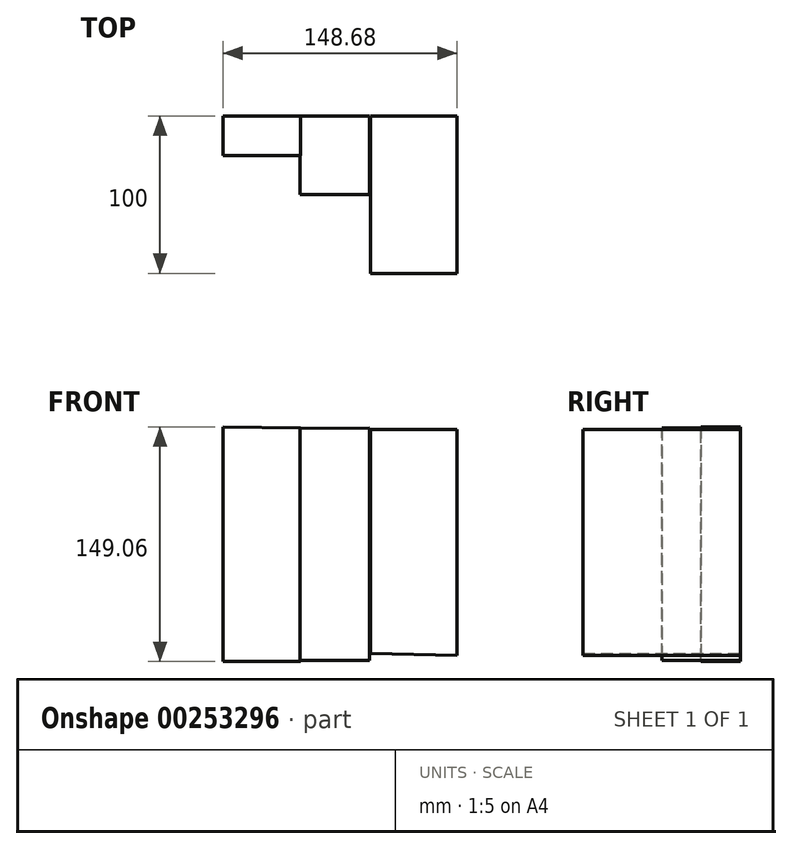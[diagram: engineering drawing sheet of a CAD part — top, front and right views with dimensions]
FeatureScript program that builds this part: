
annotation { "Feature Type Name" : "Feature", "Feature Type Description" : "" }
export const myFeature = defineFeature(function(context is Context, id is Id, definition is map)
    precondition{}
    {
        {
            var Q0;
            Q0=qCreatedBy(makeId("Front.planeOp"),FACE);
            var sketch = newSketch(context, id + "F0", { "sketchPlane" : qUnion([Q0])});
            skLineSegment(sketch, "E0", {"start": v(-74.94, 75.14) * mm, "end": v(-74.94, -73.92) * mm});
            skLineSegment(sketch, "E1", {"start": v(-74.94, -73.92) * mm, "end": v(-25.73, -73.92) * mm});
            skLineSegment(sketch, "E2", {"start": v(-25.73, -73.92) * mm, "end": v(-25.73, 74.53) * mm});
            skLineSegment(sketch, "E3", {"start": v(-25.73, 74.53) * mm, "end": v(-74.94, 75.14) * mm});
            skSolve(sketch);
        }
        {
            var Q0;
            Q0=qCreatedBy(makeId("Front.planeOp"),FACE);
            var sketch = newSketch(context, id + "F1", { "sketchPlane" : qUnion([Q0])});
            skLineSegment(sketch, "E4", {"start": v(-25.93, 74.12) * mm, "end": v(-25.93, -73.1) * mm});
            skLineSegment(sketch, "E5", {"start": v(-25.93, -73.1) * mm, "end": v(17.97, -73.1) * mm});
            skLineSegment(sketch, "E6", {"start": v(17.97, -73.1) * mm, "end": v(17.97, 74.33) * mm});
            skLineSegment(sketch, "E7", {"start": v(17.97, 74.33) * mm, "end": v(-25.93, 74.12) * mm});
            skSolve(sketch);
        }
        {
            var Q0;
            Q0=qCreatedBy(makeId("Front.planeOp"),FACE);
            var sketch = newSketch(context, id + "F2", { "sketchPlane" : qUnion([Q0])});
            skLineSegment(sketch, "E8", {"start": v(18.8, -68.76) * mm, "end": v(18.8, 73.6) * mm});
            skLineSegment(sketch, "E9", {"start": v(18.8, 73.6) * mm, "end": v(73.74, 73.6) * mm});
            skLineSegment(sketch, "E10", {"start": v(73.74, 73.6) * mm, "end": v(73.74, -69.99) * mm});
            skLineSegment(sketch, "E11", {"start": v(73.74, -69.99) * mm, "end": v(18.8, -68.76) * mm});
            skSolve(sketch);
        }
        {
            var Q0;
            Q0=makeQuery(id+"F0.imprint","IMPRINT",FACE,{"disambiguationData":[TD([[makeQuery(id+"F0.imprint","IMPRINT",EDGE,{"derivedFrom":sQuery(id+"F0.wireOp",EDGE,"E0")}),1.0]])]});
            extrude(context, id + "F3", {"entities" : qUnion([Q0]), "depth" : 25 * mm});
        }
        {
            var Q0;
            Q0=makeQuery(id+"F1.imprint","IMPRINT",FACE,{"disambiguationData":[TD([[makeQuery(id+"F1.imprint","IMPRINT",EDGE,{"derivedFrom":sQuery(id+"F1.wireOp",EDGE,"E4")}),1.0]])]});
            extrude(context, id + "F4", {"entities" : qUnion([Q0]), "operationType" : NewBodyOperationType.ADD, "depth" : 50 * mm});
        }
        {
            var Q0;
            Q0=makeQuery(id+"F2.imprint","IMPRINT",FACE,{"disambiguationData":[TD([[makeQuery(id+"F2.imprint","IMPRINT",EDGE,{"derivedFrom":sQuery(id+"F2.wireOp",EDGE,"E8")}),-1.0]])]});
            extrude(context, id + "F5", {"entities" : qUnion([Q0]), "depth" : 100 * mm});
        }
    });
